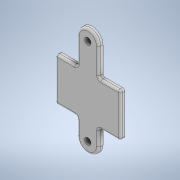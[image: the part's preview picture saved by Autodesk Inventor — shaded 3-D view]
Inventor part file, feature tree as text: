
AUTODESK INVENTOR PART (.ipt)
format: ipt  version: 2021.4 (Build 254397000, 397)  size: 176,128 bytes
history: native  units: mm
features: sketch x3, extrude x2, fillet x2, other x1, hole x1
ambient origin geometry x8: Origin, YZ Plane, XZ Plane, XY Plane, X Axis, Y Axis, Z Axis, Center Point
bodies: Body1 (feature_tree)
feature tree (9):
  other  "ソリッド1"
  extrude  "押し出し1"  Depth=60.0mm
  extrude  "押し出し2"  Depth=40.0mm
  fillet  "フィレット1"  Radius=4.0mm
  fillet  "フィレット2"  Radius=20.0mm
  hole  "穴1"  [1 undecoded]
  sketch  "スケッチ1"
  sketch  "スケッチ2"
  sketch  "スケッチ3"
note: 1 required parameter value undecoded (feature->parameter linkage not recoverable at this tier; creation-order binding heuristic only, values carry confidence <= 0.55)
